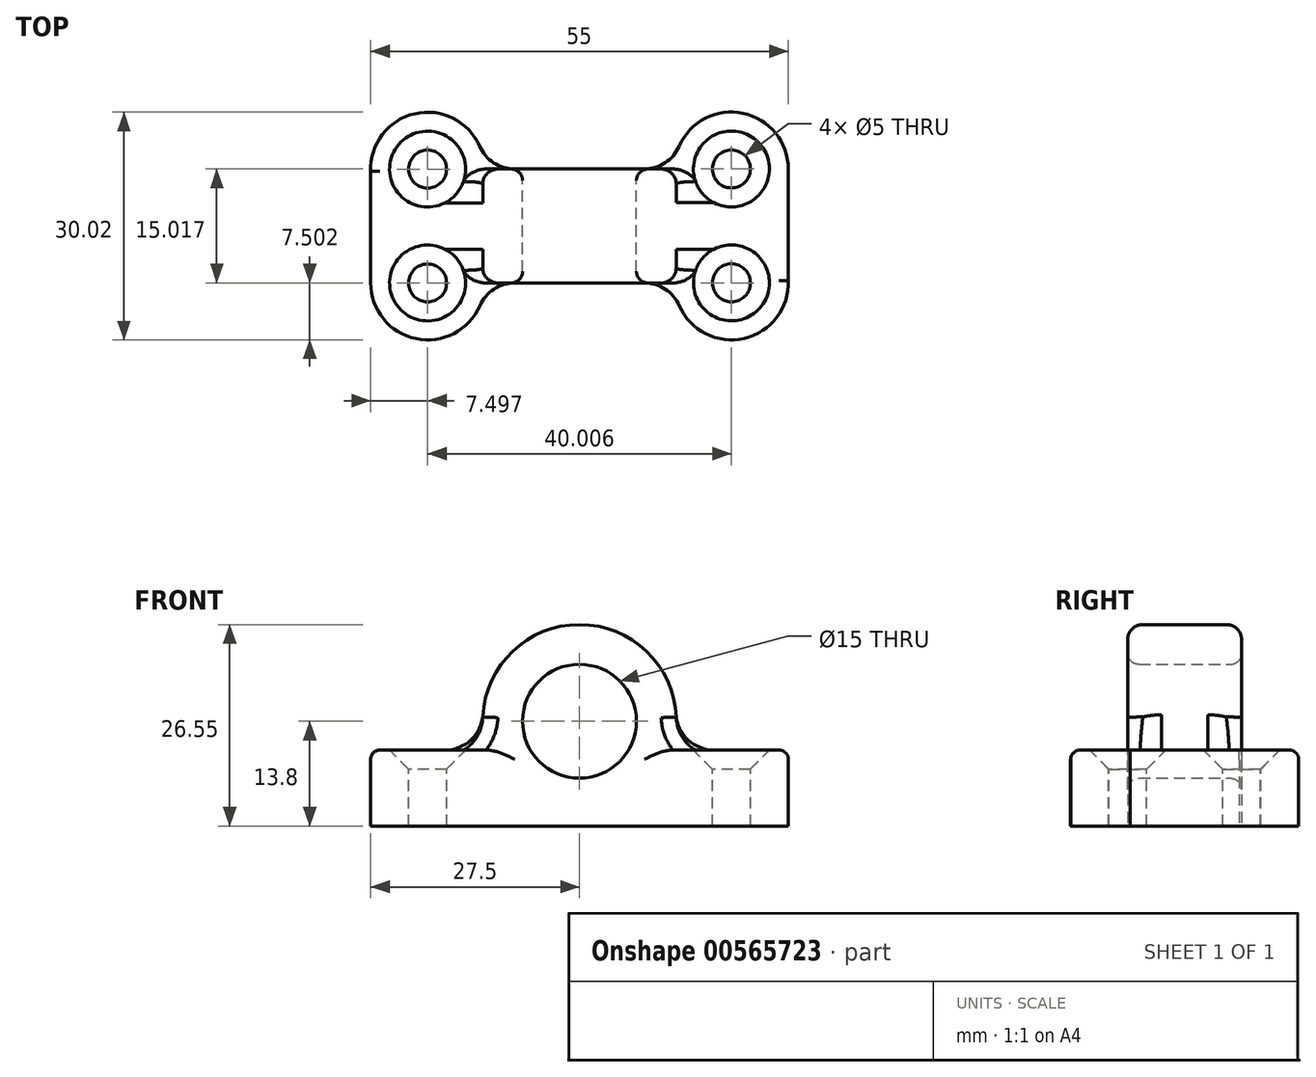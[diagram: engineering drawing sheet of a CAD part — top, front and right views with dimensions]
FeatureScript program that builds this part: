
annotation { "Feature Type Name" : "Feature", "Feature Type Description" : "" }
export const myFeature = defineFeature(function(context is Context, id is Id, definition is map)
    precondition{}
    {
        {
            var Q0;
            Q0=qCreatedBy(makeId("Top.planeOp"),FACE);
            var sketch = newSketch(context, id + "F0", { "sketchPlane" : qUnion([Q0])});
            skArc(sketch, "E0", {"start": v(-13.13, 10.5) * mm, "mid": v(-21.7, 14.8) * mm, "end": v(-27.5, 7.18) * mm});
            skLineSegment(sketch, "E1", {"start": v(0, 0) * mm, "end": v(-35.81, -0.02) * mm, "construction": true});
            skLineSegment(sketch, "E2", {"start": v(0, 0) * mm, "end": v(0, 22.8) * mm, "construction": true});
            skArc(sketch, "E3.MirrorC", {"start": v(12.5, 7.5) * mm, "mid": v(12.5, 7.5) * mm, "end": v(12.5, 7.5) * mm});
            skLineSegment(sketch, "E4.MirrorCS", {"start": v(0, 0) * mm, "end": v(35.81, 0.02) * mm, "construction": true});
            skArc(sketch, "E5.MirrorC", {"start": v(13.12, 10.5) * mm, "mid": v(21.53, 14.85) * mm, "end": v(27.5, 7.5) * mm});
            skArc(sketch, "E6.MirrorC", {"start": v(13.13, -10.5) * mm, "mid": v(21.7, -14.8) * mm, "end": v(27.5, -7.18) * mm});
            skArc(sketch, "E7.MirrorC", {"start": v(-13.12, -10.5) * mm, "mid": v(-21.53, -14.85) * mm, "end": v(-27.5, -7.5) * mm});
            skLineSegment(sketch, "E8.top", {"start": v(8.55, -7.5) * mm, "end": v(-8.54, -7.5) * mm});
            skLineSegment(sketch, "E8.left", {"start": v(27.5, 7.5) * mm, "end": v(27.5, -7.5) * mm});
            skLineSegment(sketch, "E8.right", {"start": v(-27.5, 7.5) * mm, "end": v(-27.5, -7.5) * mm});
            skPoint(sketch, "E8.middle", {"position": v(0, 0) * mm});
            skLineSegment(sketch, "E9.trimOffspring", {"start": v(8.54, 7.5) * mm, "end": v(-8.55, 7.5) * mm});
            skArc(sketch, "E10.filletArc", {"start": v(-13.13, 10.5) * mm, "mid": v(-11.29, 8.32) * mm, "end": v(-8.55, 7.5) * mm});
            skPoint(sketch, "E11.visualSharp", {"position": v(12.5, 7.5) * mm});
            skArc(sketch, "E11.filletArc", {"start": v(8.54, 7.5) * mm, "mid": v(11.28, 8.33) * mm, "end": v(13.12, 10.5) * mm});
            skPoint(sketch, "E12.visualSharp", {"position": v(-12.5, -7.5) * mm});
            skArc(sketch, "E12.filletArc", {"start": v(-8.54, -7.5) * mm, "mid": v(-11.28, -8.33) * mm, "end": v(-13.12, -10.5) * mm});
            skPoint(sketch, "E13.visualSharp", {"position": v(12.5, -7.5) * mm});
            skArc(sketch, "E13.filletArc", {"start": v(13.13, -10.5) * mm, "mid": v(11.29, -8.32) * mm, "end": v(8.55, -7.5) * mm});
            skSolve(sketch);
        }
        {
            var Q0;
            Q0=qSketchRegion(id+"F0",true);
            extrude(context, id + "F1", {"entities" : qUnion([Q0]), "depth" : 10 * mm});
        }
        {
            var Q0;
            Q0=makeQuery(id+"F1.opExtrude","CAP_FACE",FACE,{"disambiguationData":[OSD([sQuery(id+"F0.wireOp",EDGE,"E0"),sQuery(id+"F0.wireOp",EDGE,"E6.MirrorC"),sQuery(id+"F0.wireOp",EDGE,"E7.MirrorC"),sQuery(id+"F0.wireOp",EDGE,"E8.top"),sQuery(id+"F0.wireOp",EDGE,"E8.left"),sQuery(id+"F0.wireOp",EDGE,"E8.right"),sQuery(id+"F0.wireOp",EDGE,"E9.trimOffspring"),sQuery(id+"F0.wireOp",EDGE,"E10.filletArc"),sQuery(id+"F0.wireOp",EDGE,"E11.filletArc"),sQuery(id+"F0.wireOp",EDGE,"E12.filletArc"),sQuery(id+"F0.wireOp",EDGE,"E13.filletArc"),sQuery(id+"F0.wireOp",EDGE,"E5.MirrorC")])],"isStart":false});
            var sketch = newSketch(context, id + "F2", { "sketchPlane" : qUnion([Q0])});
            skPoint(sketch, "E14", {"position": v(-20, 7.5) * mm});
            skPoint(sketch, "E15", {"position": v(-20, -7.5) * mm});
            skPoint(sketch, "E16", {"position": v(20, 7.5) * mm});
            skPoint(sketch, "E17", {"position": v(20, -7.5) * mm});
            skSolve(sketch);
        }
        {
            var Q0;
            Q0=sQuery(id+"F2.wireOp",VERTEX,"E14");
            var Q1;
            Q1=sQuery(id+"F2.wireOp",VERTEX,"E16");
            var Q2;
            Q2=sQuery(id+"F2.wireOp",VERTEX,"E17");
            var Q3;
            Q3=sQuery(id+"F2.wireOp",VERTEX,"E15");
            var Q4;
            Q4=makeQuery(id+"F1.opExtrude","SWEPT_BODY",BODY,{"disambiguationData":[OSD([sQuery(id+"F0.wireOp",EDGE,"E0"),sQuery(id+"F0.wireOp",EDGE,"E6.MirrorC"),sQuery(id+"F0.wireOp",EDGE,"E7.MirrorC"),sQuery(id+"F0.wireOp",EDGE,"E8.top"),sQuery(id+"F0.wireOp",EDGE,"E8.left"),sQuery(id+"F0.wireOp",EDGE,"E8.right"),sQuery(id+"F0.wireOp",EDGE,"E9.trimOffspring"),sQuery(id+"F0.wireOp",EDGE,"E10.filletArc"),sQuery(id+"F0.wireOp",EDGE,"E11.filletArc"),sQuery(id+"F0.wireOp",EDGE,"E12.filletArc"),sQuery(id+"F0.wireOp",EDGE,"E13.filletArc"),sQuery(id+"F0.wireOp",EDGE,"E5.MirrorC")])]});
            hole(context, id + "F3", {"style" : HoleStyle.C_SINK, "endStyle" : HoleEndStyle.THROUGH, "holeDiameter" : 5 * mm, "cSinkDiameter" : 10 * mm, "cSinkAngle" : 90 * degree, "locations" : qUnion([Q0, Q1, Q2, Q3]), "scope" : qUnion([Q4]), "isTappedThrough" : true});
        }
        {
            var Q0;
            Q0=qCreatedBy(makeId("Front.planeOp"),FACE);
            var sketch = newSketch(context, id + "F4", { "sketchPlane" : qUnion([Q0])});
            skLineSegment(sketch, "E18", {"start": v(0, 0) * mm, "end": v(0, 23.41) * mm, "construction": true});
            skCircle(sketch, "E19", {"center": v(0, 13.8) * mm, "radius": 7.5 * mm});
            skArc(sketch, "E20", {"start": v(-12.75, 13.8) * mm, "mid": v(0, 26.55) * mm, "end": v(12.75, 13.8) * mm});
            skLineSegment(sketch, "E21", {"start": v(-12.75, 13.8) * mm, "end": v(-12.75, 2) * mm});
            skLineSegment(sketch, "E22", {"start": v(-12.75, 2) * mm, "end": v(12.75, 2) * mm});
            skLineSegment(sketch, "E23", {"start": v(12.75, 2) * mm, "end": v(12.75, 13.8) * mm});
            skSolve(sketch);
        }
        {
            var Q0;
            Q0=qSketchRegion(id+"F4",true);
            var Q1;
            Q1=makeQuery(id+"F1.opExtrude","SWEPT_FACE",FACE,{"disambiguationData":[OSD([sQuery(id+"F0.wireOp",EDGE,"E8.top")])]});
            var Q2;
            Q2=makeQuery(id+"F1.opExtrude","SWEPT_FACE",FACE,{"disambiguationData":[OSD([sQuery(id+"F0.wireOp",EDGE,"E9.trimOffspring")])]});
            extrude(context, id + "F5", {"entities" : qUnion([Q0]), "operationType" : NewBodyOperationType.ADD, "endBound" : BoundingType.UP_TO_SURFACE, "endBoundEntityFace" : qUnion([Q1]), "depth" : 25 * mm, "hasSecondDirection" : true, "secondDirectionBound" : SecondDirectionBoundingType.UP_TO_SURFACE, "secondDirectionOppositeDirection" : true, "secondDirectionBoundEntityFace" : qUnion([Q2]), "secondDirectionDepth" : 25 * mm});
        }
        {
            var Q0;
            Q0=makeQuery(id+"F5.boolean.opBoolean","INTERSECT",EDGE,{"derivedFrom":[makeQuery(id+"F1.opExtrude","CAP_FACE",FACE,{"disambiguationData":[OSD([sQuery(id+"F0.wireOp",EDGE,"E0"),sQuery(id+"F0.wireOp",EDGE,"E6.MirrorC"),sQuery(id+"F0.wireOp",EDGE,"E7.MirrorC"),sQuery(id+"F0.wireOp",EDGE,"E8.top"),sQuery(id+"F0.wireOp",EDGE,"E8.left"),sQuery(id+"F0.wireOp",EDGE,"E8.right"),sQuery(id+"F0.wireOp",EDGE,"E9.trimOffspring"),sQuery(id+"F0.wireOp",EDGE,"E10.filletArc"),sQuery(id+"F0.wireOp",EDGE,"E11.filletArc"),sQuery(id+"F0.wireOp",EDGE,"E12.filletArc"),sQuery(id+"F0.wireOp",EDGE,"E13.filletArc"),sQuery(id+"F0.wireOp",EDGE,"E5.MirrorC")])],"isStart":false}),makeQuery(id+"F5.opExtrude","SWEPT_FACE",FACE,{"disambiguationData":[OSD([sQuery(id+"F4.wireOp",EDGE,"E23")])]})]});
            var Q1;
            Q1=makeQuery(id+"F5.boolean.opBoolean","INTERSECT",EDGE,{"derivedFrom":[makeQuery(id+"F1.opExtrude","CAP_FACE",FACE,{"disambiguationData":[OSD([sQuery(id+"F0.wireOp",EDGE,"E0"),sQuery(id+"F0.wireOp",EDGE,"E6.MirrorC"),sQuery(id+"F0.wireOp",EDGE,"E7.MirrorC"),sQuery(id+"F0.wireOp",EDGE,"E8.top"),sQuery(id+"F0.wireOp",EDGE,"E8.left"),sQuery(id+"F0.wireOp",EDGE,"E8.right"),sQuery(id+"F0.wireOp",EDGE,"E9.trimOffspring"),sQuery(id+"F0.wireOp",EDGE,"E10.filletArc"),sQuery(id+"F0.wireOp",EDGE,"E11.filletArc"),sQuery(id+"F0.wireOp",EDGE,"E12.filletArc"),sQuery(id+"F0.wireOp",EDGE,"E13.filletArc"),sQuery(id+"F0.wireOp",EDGE,"E5.MirrorC")])],"isStart":false}),makeQuery(id+"F5.opExtrude","SWEPT_FACE",FACE,{"disambiguationData":[OSD([sQuery(id+"F4.wireOp",EDGE,"E21")])]})]});
            fillet(context, id + "F6", {"entities" : qUnion([Q0, Q1]), "radius" : 5 * mm, "tangentPropagation" : true, "allowEdgeOverflow" : false});
        }
        {
            var Q0;
            Q0=makeQuery(id+"F4.imprint","IMPRINT",FACE,{"disambiguationData":[TD([[makeQuery(id+"F4.imprint","IMPRINT",EDGE,{"derivedFrom":sQuery(id+"F4.wireOp",EDGE,"E19")}),1.0]])]});
            extrude(context, id + "F7", {"entities" : qUnion([Q0]), "operationType" : NewBodyOperationType.REMOVE, "endBound" : BoundingType.SYMMETRIC, "oppositeDirection" : true, "depth" : 25 * mm, "offsetDistance" : 25 * mm});
        }
        {
            var Q0;
            {var subQ0=sQuery(id+"F4.wireOp",EDGE,"E19");Q0=makeQuery(id+"F7.boolean.opBoolean","INTERSECT",EDGE,{"derivedFrom":[makeQuery(id+"F5.boolean.opBoolean","MERGE",FACE,{"derivedFrom":[makeQuery(id+"F1.opExtrude","SWEPT_FACE",FACE,{"disambiguationData":[OSD([sQuery(id+"F0.wireOp",EDGE,"E8.top")])]}),makeQuery(id+"F5.opExtrude","CAP_FACE",FACE,{"disambiguationData":[OSD([subQ0,sQuery(id+"F4.wireOp",EDGE,"E20"),sQuery(id+"F4.wireOp",EDGE,"E21"),sQuery(id+"F4.wireOp",EDGE,"E22"),sQuery(id+"F4.wireOp",EDGE,"E23")])],"isStart":false})]}),makeQuery(id+"F7.opExtrude","SWEPT_FACE",FACE,{"disambiguationData":[OSD([subQ0])]})]});}
            var Q1;
            {var subQ0=sQuery(id+"F4.wireOp",EDGE,"E19");Q1=makeQuery(id+"F7.boolean.opBoolean","INTERSECT",EDGE,{"derivedFrom":[makeQuery(id+"F5.boolean.opBoolean","MERGE",FACE,{"derivedFrom":[makeQuery(id+"F1.opExtrude","SWEPT_FACE",FACE,{"disambiguationData":[OSD([sQuery(id+"F0.wireOp",EDGE,"E9.trimOffspring")])]}),makeQuery(id+"F5.opExtrude","CAP_FACE",FACE,{"disambiguationData":[OSD([subQ0,sQuery(id+"F4.wireOp",EDGE,"E20"),sQuery(id+"F4.wireOp",EDGE,"E21"),sQuery(id+"F4.wireOp",EDGE,"E22"),sQuery(id+"F4.wireOp",EDGE,"E23")])],"isStart":true})]}),makeQuery(id+"F7.opExtrude","SWEPT_FACE",FACE,{"disambiguationData":[OSD([subQ0])]})]});}
            fillet(context, id + "F8", {"entities" : qUnion([Q0, Q1]), "radius" : 1.5 * mm, "allowEdgeOverflow" : false});
        }
        {
            var Q0;
            Q0=makeQuery(id+"F5.opExtrude","CAP_EDGE",EDGE,{"disambiguationData":[OSD([sQuery(id+"F4.wireOp",EDGE,"E20")])],"isStart":false});
            var Q1;
            Q1=makeQuery(id+"F5.opExtrude","CAP_EDGE",EDGE,{"disambiguationData":[OSD([sQuery(id+"F4.wireOp",EDGE,"E20")])],"isStart":true});
            fillet(context, id + "F9", {"entities" : qUnion([Q0, Q1]), "radius" : 2 * mm, "tangentPropagation" : true, "allowEdgeOverflow" : false});
        }
        {
            var Q0;
            Q0=makeQuery(id+"F1.opExtrude","CAP_EDGE",EDGE,{"disambiguationData":[OSD([sQuery(id+"F0.wireOp",EDGE,"E12.filletArc")])],"isStart":false});
            var Q1;
            Q1=makeQuery(id+"F1.opExtrude","CAP_EDGE",EDGE,{"disambiguationData":[OSD([sQuery(id+"F0.wireOp",EDGE,"E10.filletArc")])],"isStart":false});
            var Q2;
            Q2=makeQuery(id+"F1.opExtrude","CAP_EDGE",EDGE,{"disambiguationData":[OSD([sQuery(id+"F0.wireOp",EDGE,"E13.filletArc")])],"isStart":false});
            var Q3;
            Q3=makeQuery(id+"F1.opExtrude","CAP_EDGE",EDGE,{"disambiguationData":[OSD([sQuery(id+"F0.wireOp",EDGE,"E11.filletArc")])],"isStart":false});
            fillet(context, id + "F10", {"entities" : qUnion([Q0, Q1, Q2, Q3]), "radius" : 1.2 * mm, "tangentPropagation" : true, "allowEdgeOverflow" : false});
        }
    });
